# Revit family: 931000001_Desague Automico CR
name_source: partatom
category: Plumbing Fixtures
units: mm (PartAtom-declared; Revit-internal decimal feet)

## family parameters
Always vertical = Yes
Cut with Voids When Loaded = No
OmniClass Number = 23.45.00.00
Part Type = Normal
Room Calculation Point = No
Round Connector Dimension = Use Diameter
Shared = No
Work Plane-Based = No

## types (2) — shared parameters
Description = Para la fabricación de este producto se utilizan materiales, equipos 
y tecnologías de última generación, que permiten ofrecer un artículo 
con los más altos estándares de calidad.
Manufacturer = Grival
Material = Corona_Plastico_Gris
Material 2 = Corona_Plastico_Cromado
Material 3 = Corona_Plastico_Negro
Material 4 = Corona_Plastico_Blanco
Normatividad = Norma IAPMO IGC 157.
Recubrimientos = -Resistente a la corrosión, pelado y decoloración por agua. -Resistente al efecto de jabones y limpiadores de tocador. -Recubrimientos no tóxico. -Condición de servicio recomendada, uso doméstico.
URL = https://www.grival.com
zero-valued in all types: Default Elevation

## per-type parameters (varying)
| type | Referencia |
| Desagüe Automatico | 931000001 |
| Desagüe Automatico Sin Rebose | 931110001 |

note: column(s) folded — value = type name in every type: Model

type visibility flags: 2 boolean params named "<type name>" — each type sets only its own to Yes (folded from table)

## geometry (parser evidence)
native form markers: Sweep x5
no freeform markers — native parametric forms only
